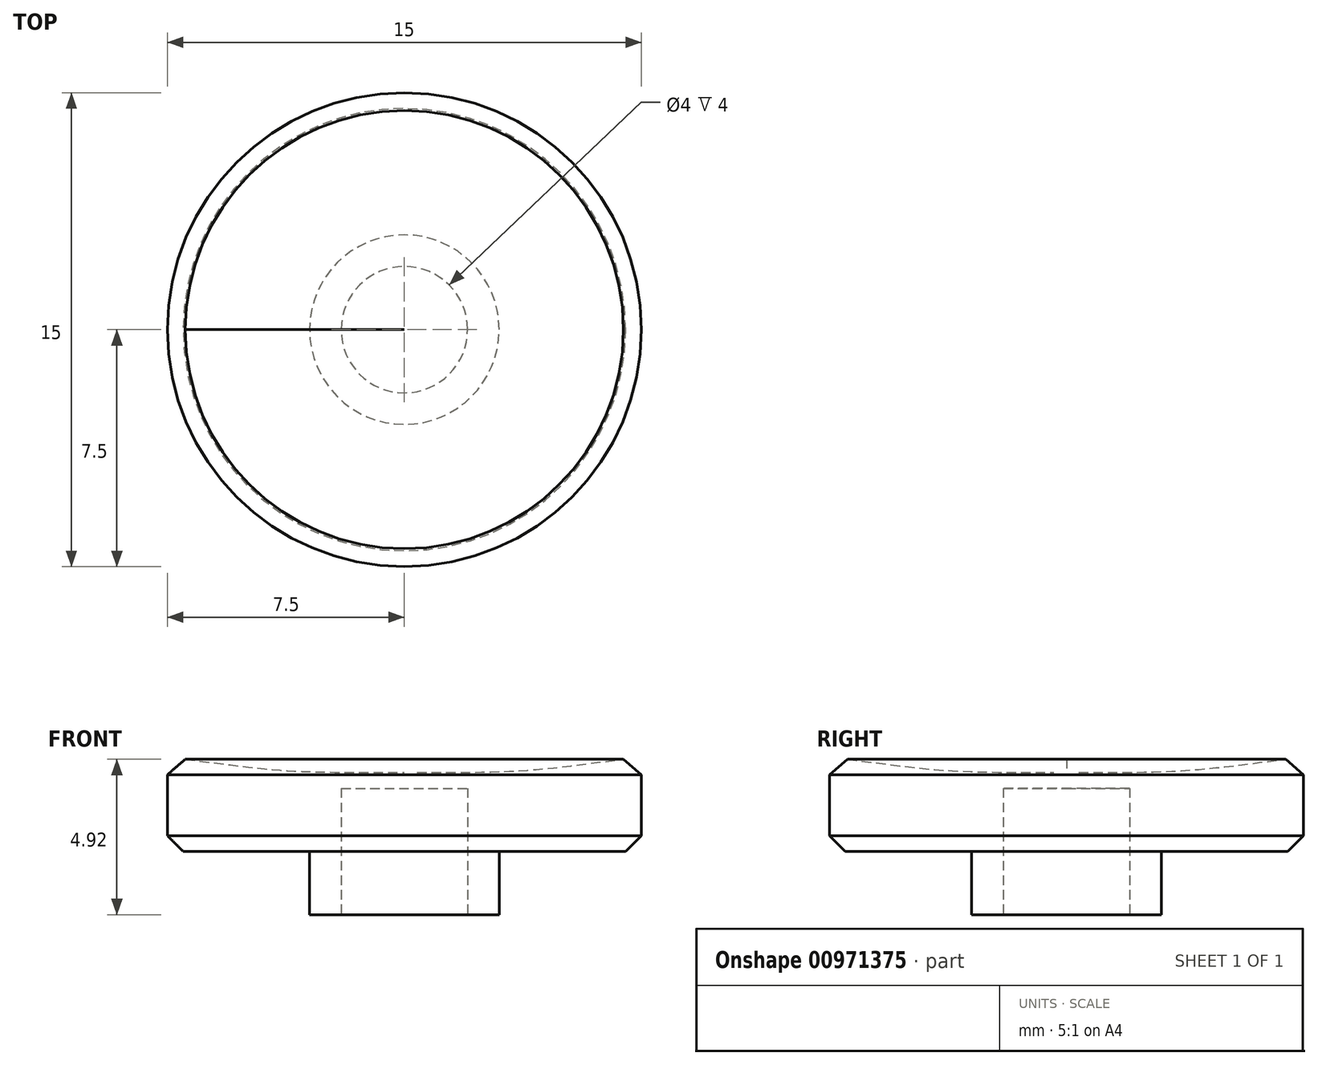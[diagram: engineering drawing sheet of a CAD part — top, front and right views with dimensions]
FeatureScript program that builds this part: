
annotation { "Feature Type Name" : "Feature", "Feature Type Description" : "" }
export const myFeature = defineFeature(function(context is Context, id is Id, definition is map)
    precondition{}
    {
        {
            var Q0;
            Q0=qCreatedBy(makeId("Front.planeOp"),FACE);
            var sketch = newSketch(context, id + "F0", { "sketchPlane" : qUnion([Q0])});
            skLineSegment(sketch, "E0", {"start": v(-2, 0) * mm, "end": v(-2, 2) * mm});
            skLineSegment(sketch, "E1", {"start": v(-2, 2) * mm, "end": v(0, 2) * mm});
            skLineSegment(sketch, "E2", {"start": v(0, 3) * mm, "end": v(-7.5, 3) * mm, "construction": true});
            skLineSegment(sketch, "E3", {"start": v(-7.5, 3) * mm, "end": v(-7.5, 0) * mm});
            skPoint(sketch, "E4", {"position": v(0, 2.5) * mm});
            skFitSpline(sketch, "E5", {"points": [v(-7.5, 3) * mm, v(0, 2.5) * mm], "startDerivative": vector(11.25, -1.5) * mm, "endDerivative": vector(11.25, 0) * mm});
            skLineSegment(sketch, "E6", {"start": v(0, 2.5) * mm, "end": v(-7.5, 2.5) * mm, "construction": true});
            skLineSegment(sketch, "E7", {"start": v(0, 2) * mm, "end": v(0, 2.5) * mm});
            skLineSegment(sketch, "E8", {"start": v(0, 3) * mm, "end": v(0, 2.5) * mm, "construction": true});
            skLineSegment(sketch, "E9", {"start": v(-2, 0) * mm, "end": v(-2, -2) * mm});
            skLineSegment(sketch, "E10", {"start": v(-2, -2) * mm, "end": v(-3, -2) * mm});
            skLineSegment(sketch, "E11", {"start": v(-3, -2) * mm, "end": v(-3, 0) * mm});
            skLineSegment(sketch, "E12", {"start": v(-3, 0) * mm, "end": v(-7.5, 0) * mm});
            skLineSegment(sketch, "E13", {"start": v(-3, 0) * mm, "end": v(-2, 0) * mm, "construction": true});
            skSolve(sketch);
        }
        {
            var Q0;
            Q0=makeQuery(id+"F0.imprint","IMPRINT",FACE,{"disambiguationData":[TD([[makeQuery(id+"F0.imprint","IMPRINT",EDGE,{"derivedFrom":sQuery(id+"F0.wireOp",EDGE,"E0")}),1.0]])]});
            var Q1;
            Q1=sQuery(id+"F0.wireOp",EDGE,"E7");
            revolve(context, id + "F1", {"surfaceOperationType" : NewSurfaceOperationType.NEW, "entities" : qUnion([Q0]), "axis" : qUnion([Q1]), "revolveType" : RevolveType.FULL});
        }
        {
            var Q0;
            Q0=makeQuery(id+"F1.opRevolve","SWEPT_EDGE",EDGE,{"disambiguationData":[OSD([sQuery(id+"F0.wireOp",EDGE,"E3"),sQuery(id+"F0.wireOp",EDGE,"G3t3IqTW-xWnE-snQL-XWdu-i9nqf6YtAog2")])]});
            var Q1;
            Q1=makeQuery(id+"F1.opRevolve","SWEPT_FACE",FACE,{"disambiguationData":[OSD([sQuery(id+"F0.wireOp",EDGE,"E5")])]});
            chamfer(context, id + "F2", {"entities" : qUnion([Q0, Q1]), "width" : .5 * mm, "tangentPropagation" : true});
        }
    });
